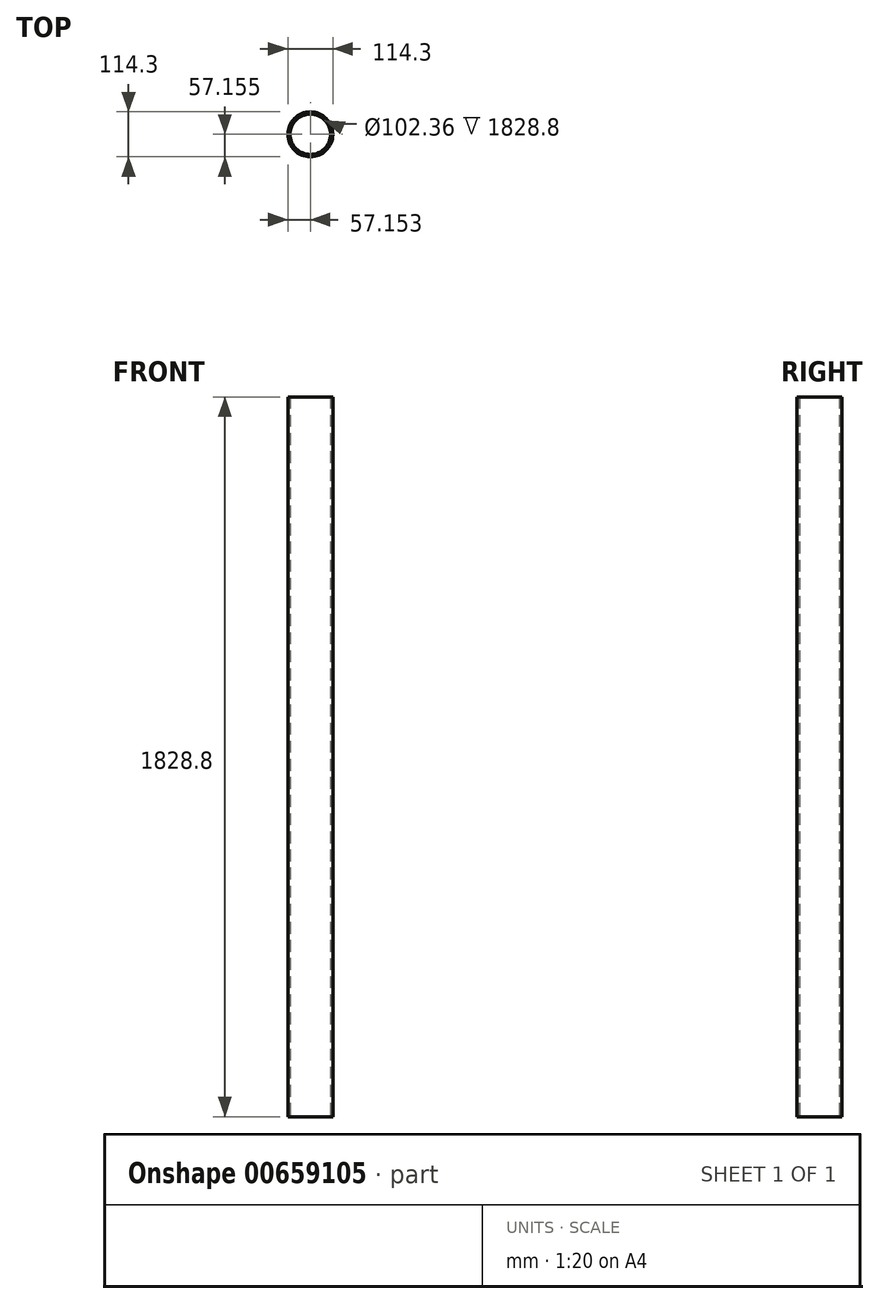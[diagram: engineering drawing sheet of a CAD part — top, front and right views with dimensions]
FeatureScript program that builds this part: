
annotation { "Feature Type Name" : "Feature", "Feature Type Description" : "" }
export const myFeature = defineFeature(function(context is Context, id is Id, definition is map)
    precondition{}
    {
        {
            var Q0;
            Q0=qCreatedBy(makeId("Top.planeOp"),FACE);
            var sketch = newSketch(context, id + "F0", { "sketchPlane" : qUnion([Q0])});
            skCircle(sketch, "E0", {"center": v(-58.56, 38.74) * mm, "radius": 57.15 * mm});
            skCircle(sketch, "E1", {"center": v(-58.56, 38.74) * mm, "radius": 51.18 * mm});
            skSolve(sketch);
        }
        {
            var Q0;
            Q0=makeQuery(id+"F0.imprint","IMPRINT",FACE,{"disambiguationData":[TD([[makeQuery(id+"F0.imprint","IMPRINT",EDGE,{"derivedFrom":sQuery(id+"F0.wireOp",EDGE,"E0")}),1.0]])]});
            extrude(context, id + "F1", {"entities" : qUnion([Q0]), "depth" : 1828.8 * mm, "offsetDistance" : 25.4 * mm});
        }
    });
